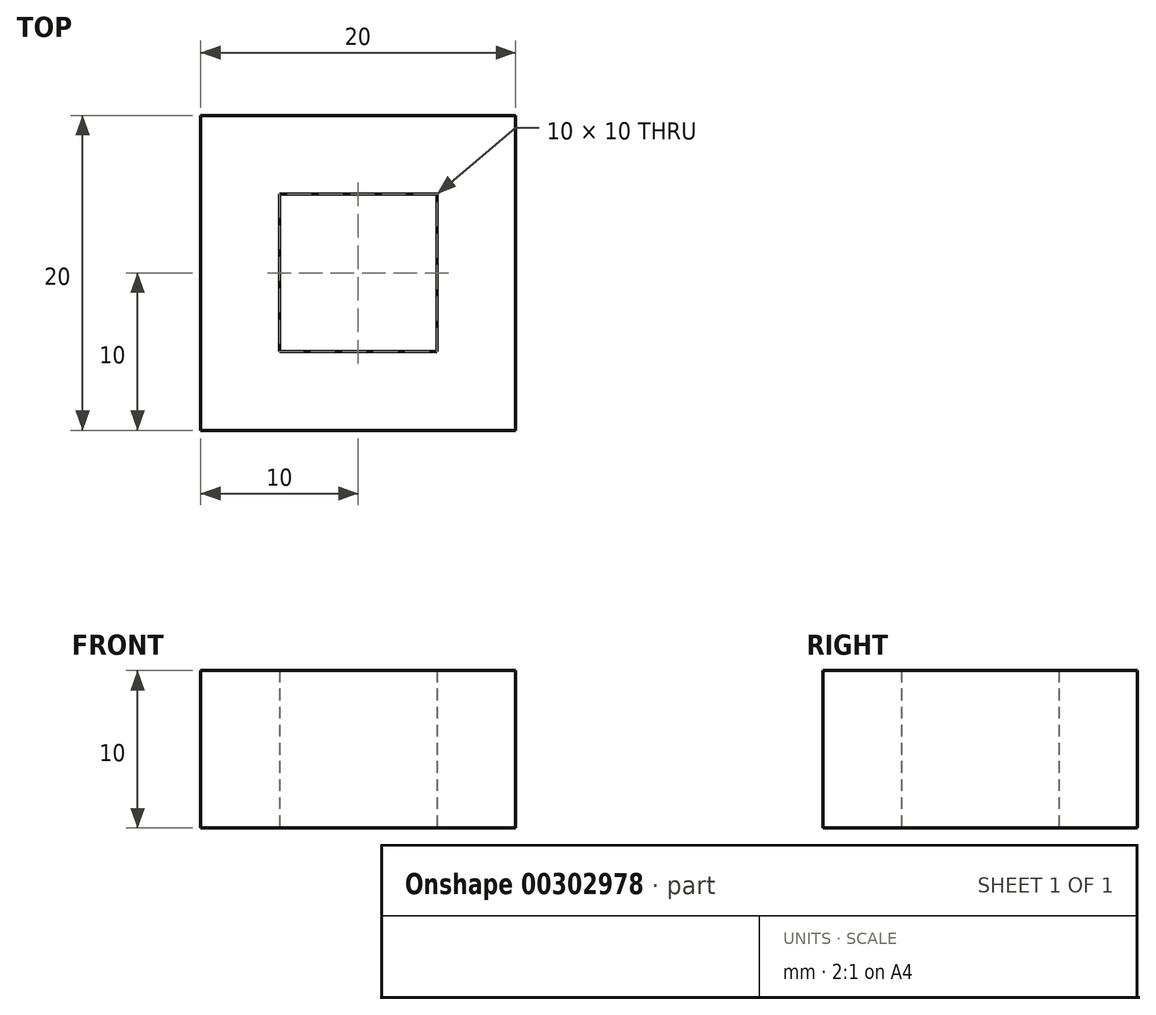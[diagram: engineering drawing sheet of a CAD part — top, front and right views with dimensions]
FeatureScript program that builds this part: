
annotation { "Feature Type Name" : "Feature", "Feature Type Description" : "" }
export const myFeature = defineFeature(function(context is Context, id is Id, definition is map)
    precondition{}
    {
        {
            var Q0;
            Q0=qCreatedBy(makeId("Top.planeOp"),FACE);
            var sketch = newSketch(context, id + "F0", { "sketchPlane" : qUnion([Q0])});
            skLineSegment(sketch, "E0.bottom", {"start": v(5, 5) * mm, "end": v(-5, 5) * mm});
            skLineSegment(sketch, "E0.top", {"start": v(5, -5) * mm, "end": v(-5, -5) * mm});
            skLineSegment(sketch, "E0.left", {"start": v(5, 5) * mm, "end": v(5, -5) * mm});
            skLineSegment(sketch, "E0.right", {"start": v(-5, 5) * mm, "end": v(-5, -5) * mm});
            skPoint(sketch, "E0.middle", {"position": v(0, 0) * mm});
            skLineSegment(sketch, "E1.bottom", {"start": v(10, 10) * mm, "end": v(-10, 10) * mm});
            skLineSegment(sketch, "E1.top", {"start": v(10, -10) * mm, "end": v(-10, -10) * mm});
            skLineSegment(sketch, "E1.left", {"start": v(10, 10) * mm, "end": v(10, -10) * mm});
            skLineSegment(sketch, "E1.right", {"start": v(-10, 10) * mm, "end": v(-10, -10) * mm});
            skSolve(sketch);
        }
        {
            var Q0;
            Q0=makeQuery(id+"F0.imprint","IMPRINT",FACE,{"disambiguationData":[TD([[makeQuery(id+"F0.imprint","IMPRINT",EDGE,{"derivedFrom":sQuery(id+"F0.wireOp",EDGE,"E0.bottom")}),-1.0]])]});
            extrude(context, id + "F1", {"entities" : qUnion([Q0]), "depth" : 10 * mm, "offsetDistance" : 25 * mm});
        }
    });
